# Revit family: NOK1_63_UN_Surface-mounted_ETK
name_source: partatom
category: Lighting Fixtures
units: mm (PartAtom-declared; Revit-internal decimal feet)

## family parameters
Always vertical = Yes
Cut with Voids When Loaded = Yes
Light Source = Yes
OmniClass Number = 23.80.70.11.14.11
OmniClass Title = Downlights
Part Type = Normal
Room Calculation Point = Yes
Round Connector Dimension = Use Diameter
Shared = No
Work Plane-Based = No

## types (6) — shared parameters
Apparent Load = 24 VA
Assembly Code = 63.0
Calc_LightSource = 160 mm  [stored 0.524934 ft]
Calc_Radius = 55 mm  [stored 0.180446 ft]
Calc_Symbol_Diameter = 1 mm  [stored 0.00328084 ft]
Color Filter = 16777215
D1 = 110 mm  [stored 0.360892 ft]
Dimming Lamp Color Temperature Shift = <None>
ETIM Code = -
GTIN Code = -
Housing_Material = Select RGB Value for different appearance
IK Value = -
IP Value = IP40
ISBN Code = -
IfcExportAs = IfcLightFixtureType
IfcExportType = USERDEFINED
L1 = 165 mm  [stored 0.541339 ft]
Lamp = LED
Manufacturer = ETK B.V.
Model = NOK.1
Tilt Angle = 90.00°
Type Comments = NOK.1 Delta
URL = https://www.ivlibrary.com
Voltage = 230 V
Wattage Comments = 24

## per-type parameters (varying)
| type | Luminous Flux (lm) | Photometric Web File |
| NOK.1 LED 24W 4000K 36 3680Lm CRI>80 wit DALI 110x165 | 2699 lm | NOK.1203.15.ies |
| NOK.1 LED 24W 4000K 36 3680Lm CRI>80 zwart DALI 110x165 | 2699 lm | NOK.1203.31.ies |
| NOK.1 LED 24W 3000K 36 3580Lm CRI>80 zwart DALI 110x165 | 2603 lm | NOK.1103.31.ies |
| NOK.1 LED 24W 4000K 36 3680Lm CRI>80 zwart 110x165 | 2699 lm | NOK.1200.31.ies |
| NOK.1 LED 24W 3000K 36 3580Lm CRI>80 zwart 110x165 | 2603 lm | NOK.1100.31.ies |
| NOK.1 LED 24W 4000K 36 3680Lm CRI>80 wit 110x165 | 2699 lm | NOK.1200.15.ies |

note: [stored X ft] marks values corroborated as IEEE doubles in the binary element streams (Revit-internal decimal feet)

## geometry (parser evidence)
native form markers: Sweep x4
no freeform markers — native parametric forms only
